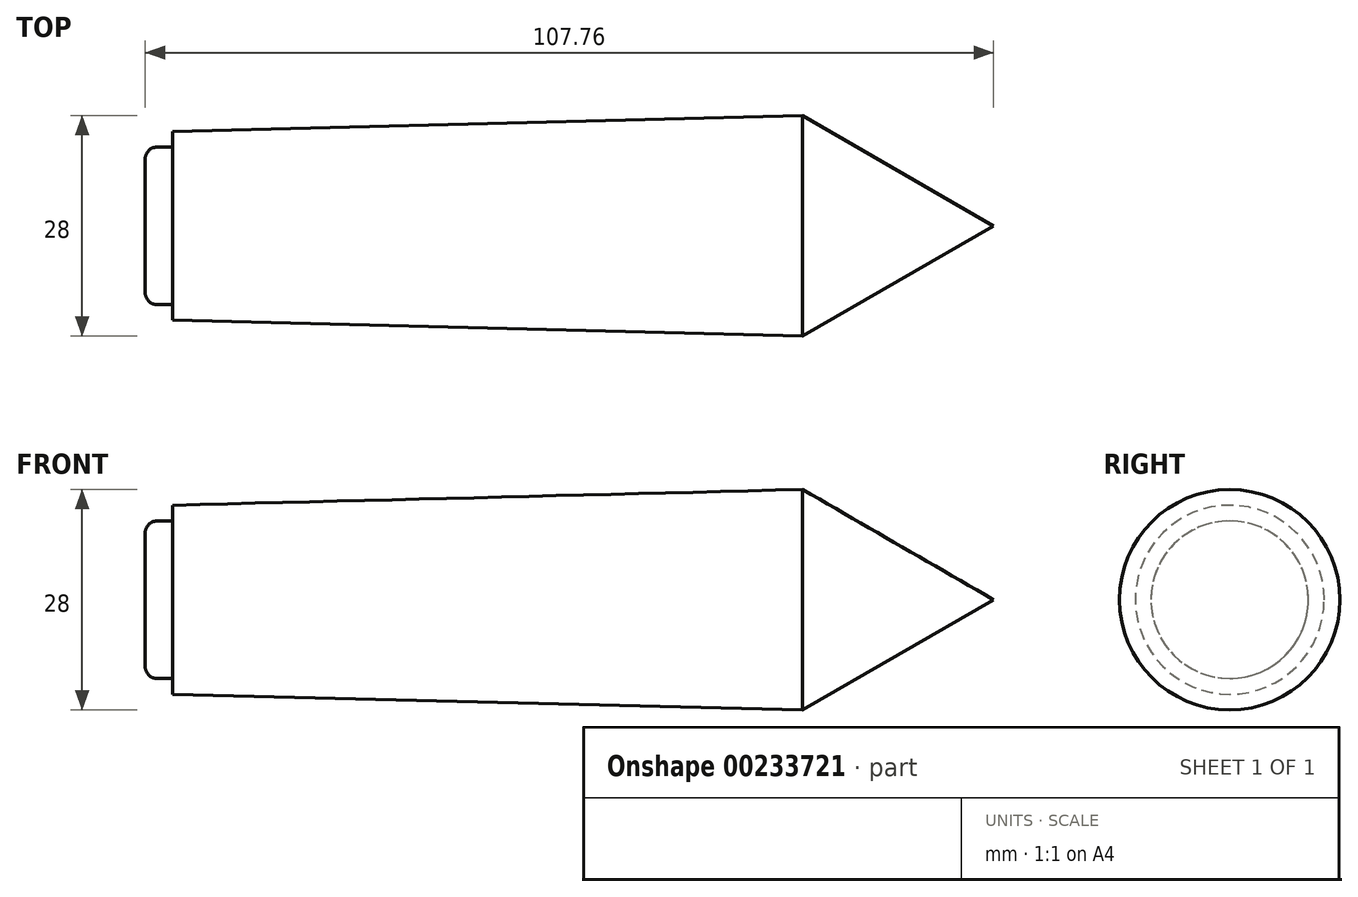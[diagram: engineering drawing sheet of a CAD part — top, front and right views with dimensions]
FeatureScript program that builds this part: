
annotation { "Feature Type Name" : "Feature", "Feature Type Description" : "" }
export const myFeature = defineFeature(function(context is Context, id is Id, definition is map)
    precondition{}
    {
        {
            var Q0;
            Q0=qCreatedBy(makeId("Front.planeOp"),FACE);
            var sketch = newSketch(context, id + "F0", { "sketchPlane" : qUnion([Q0])});
            skLineSegment(sketch, "E0", {"start": v(23.58, 14) * mm, "end": v(47.83, 0) * mm});
            skLineSegment(sketch, "E1", {"start": v(47.83, 0) * mm, "end": v(23.58, -14) * mm});
            skLineSegment(sketch, "E2", {"start": v(23.58, -14) * mm, "end": v(23.58, 14) * mm});
            skLineSegment(sketch, "E3", {"start": v(-56.42, 12) * mm, "end": v(-56.42, -12) * mm});
            skLineSegment(sketch, "E4", {"start": v(-76.06, 0) * mm, "end": v(68.76, 0) * mm});
            skLineSegment(sketch, "E5", {"start": v(-56.42, -12) * mm, "end": v(23.58, -14) * mm});
            skLineSegment(sketch, "E6", {"start": v(-56.42, 12) * mm, "end": v(23.58, 14) * mm});
            skLineSegment(sketch, "E7", {"start": v(-56.42, 10) * mm, "end": v(-59.93, 10) * mm});
            skLineSegment(sketch, "E8", {"start": v(-59.93, 10) * mm, "end": v(-59.93, -10) * mm});
            skLineSegment(sketch, "E9", {"start": v(-59.93, -10) * mm, "end": v(-56.42, -10) * mm});
            skSolve(sketch);
        }
        {
            var Q0;
            {var subQ0=sQuery(id+"F0.wireOp",EDGE,"E0");Q0=makeQuery(id+"F0.imprint","IMPRINT",FACE,{"disambiguationData":[TD([[makeQuery(id+"F0.imprint","IMPRINT",EDGE,{"derivedFrom":subQ0}),-1.0]])]});}
            var Q1;
            Q1=sQuery(id+"F0.wireOp",EDGE,"E4");
            revolve(context, id + "F1", {"entities" : qUnion([Q0]), "axis" : qUnion([Q1]), "revolveType" : RevolveType.FULL});
        }
        {
            var Q0;
            {var subQ6=sQuery(id+"F0.wireOp",EDGE,"E6");Q0=makeQuery(id+"F0.imprint","IMPRINT",FACE,{"disambiguationData":[TD([[makeQuery(id+"F0.imprint","IMPRINT",EDGE,{"derivedFrom":subQ6}),-1.0]])]});}
            var Q1;
            Q1=sQuery(id+"F0.wireOp",EDGE,"E4");
            revolve(context, id + "F2", {"entities" : qUnion([Q0]), "axis" : qUnion([Q1]), "revolveType" : RevolveType.FULL});
        }
        {
            var Q0;
            {var subQ0=sQuery(id+"F0.wireOp",EDGE,"E7");Q0=makeQuery(id+"F0.imprint","IMPRINT",FACE,{"disambiguationData":[TD([[makeQuery(id+"F0.imprint","IMPRINT",EDGE,{"derivedFrom":subQ0}),1.0]])]});}
            var Q1;
            Q1=sQuery(id+"F0.wireOp",EDGE,"E4");
            revolve(context, id + "F3", {"entities" : qUnion([Q0]), "axis" : qUnion([Q1]), "revolveType" : RevolveType.FULL});
        }
        {
            var Q0;
            Q0=makeQuery(id+"F3.opRevolve","SWEPT_EDGE",EDGE,{"disambiguationData":[OSD([sQuery(id+"F0.wireOp",EDGE,"E7"),sQuery(id+"F0.wireOp",EDGE,"E8")])]});
            fillet(context, id + "F4", {"entities" : qUnion([Q0]), "radius" : 1.5 * mm, "tangentPropagation" : true, "allowEdgeOverflow" : false});
        }
    });
